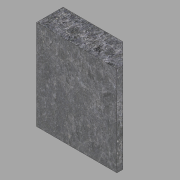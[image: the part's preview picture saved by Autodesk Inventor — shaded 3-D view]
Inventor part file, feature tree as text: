
AUTODESK INVENTOR PART (.ipt)
format: ipt  version: 2022.2 (Build 262287000, 287)  size: 124,928 bytes
history: native  units: in
note: dims shown in document units (in); Inventor stores cm internally (conversion verified against a paired STEP export)
features: extrude x2, sketch x2
ambient origin geometry x8: Origin, YZ Plane, XZ Plane, XY Plane, X Axis, Y Axis, Z Axis, Center Point
bodies: Solid1 (feature_tree)
feature tree (4):
  extrude  "Extrusion1"  Depth=7.625in
  extrude  "Extrusion3"  TaperAngle=45.0deg  [1 undecoded]
  sketch  "Sketch1"  dims[d0=2.25in d1=7.625in]
  sketch  "Sketch3"  dims[d2=6.8125in d3=0.0in d9=45.0deg d10=0.5in d11=1.75in d12=1.0in d13=0.0in]
note: 1 required parameter value undecoded (feature->parameter linkage not recoverable at this tier; creation-order binding heuristic only, values carry confidence <= 0.55)
